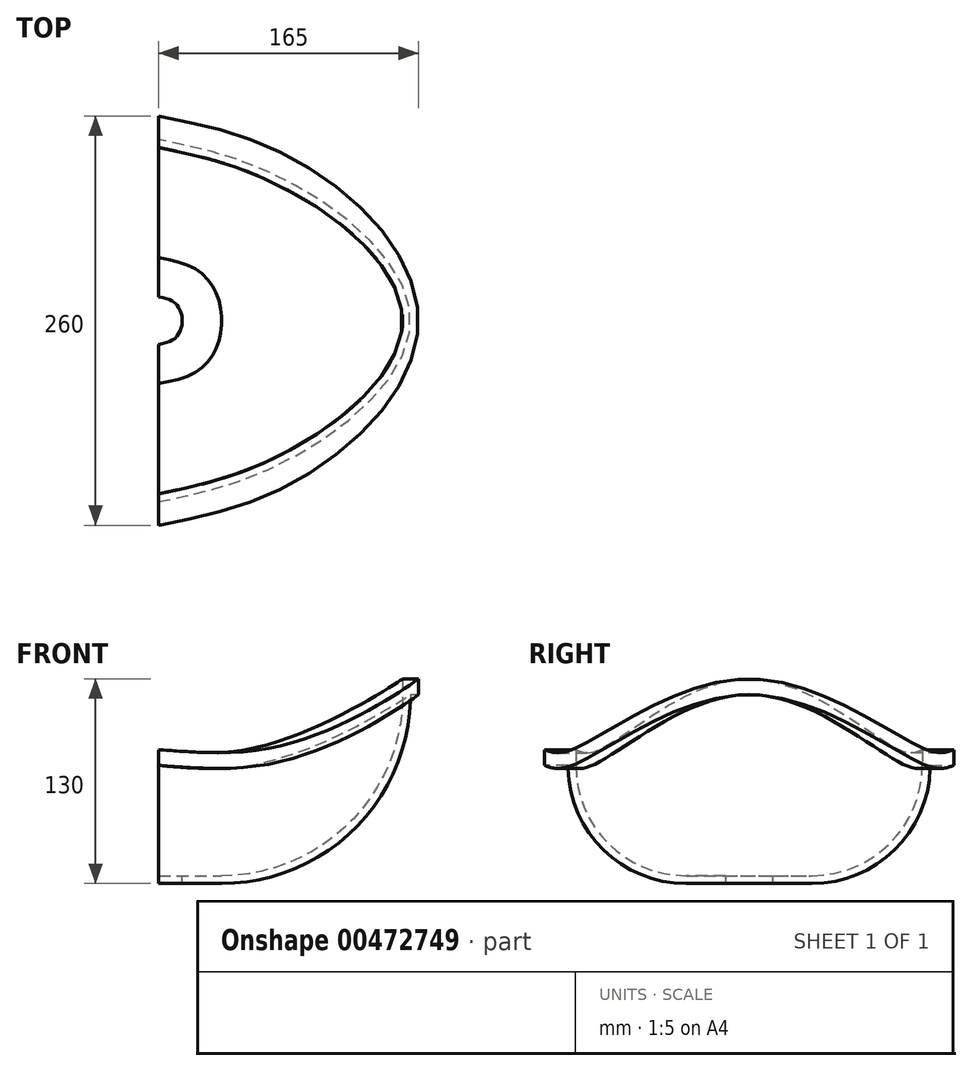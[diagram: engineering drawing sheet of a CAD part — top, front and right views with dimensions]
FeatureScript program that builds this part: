
annotation { "Feature Type Name" : "Feature", "Feature Type Description" : "" }
export const myFeature = defineFeature(function(context is Context, id is Id, definition is map)
    precondition{}
    {
        {
            var Q0;
            Q0=qCreatedBy(makeId("Front.planeOp"),FACE);
            var sketch = newSketch(context, id + "F0", { "sketchPlane" : qUnion([Q0])});
            skLineSegment(sketch, "E0.bottom", {"start": v(15, 5) * mm, "end": v(40, 5) * mm});
            skLineSegment(sketch, "E0.top", {"start": v(15, 0) * mm, "end": v(40, 0) * mm});
            skLineSegment(sketch, "E0.left", {"start": v(15, 5) * mm, "end": v(15, 0) * mm});
            skLineSegment(sketch, "E0.right", {"start": v(40, 5) * mm, "end": v(40, 0) * mm});
            skLineSegment(sketch, "E1.bottom", {"start": v(155, 130) * mm, "end": v(165, 130) * mm});
            skLineSegment(sketch, "E1.top", {"start": v(155, 120) * mm, "end": v(165, 120) * mm});
            skLineSegment(sketch, "E1.left", {"start": v(155, 130) * mm, "end": v(155, 120) * mm});
            skLineSegment(sketch, "E1.right", {"start": v(165, 130) * mm, "end": v(165, 120) * mm});
            skArc(sketch, "E2", {"start": v(40, 0) * mm, "mid": v(124.85, 35.15) * mm, "end": v(160, 120) * mm});
            skArc(sketch, "E3", {"start": v(40, 5) * mm, "mid": v(121.32, 38.68) * mm, "end": v(155, 120) * mm});
            skLineSegment(sketch, "E4", {"start": v(0, 0) * mm, "end": v(0, 50) * mm, "construction": true});
            skSolve(sketch);
        }
        {
            var Q0;
            Q0=sQuery(id+"F0.wireOp",EDGE,"E4");
            cPlane(context, id + "F1", {"entities" : qUnion([Q0]), "cplaneType" : CPlaneType.LINE_ANGLE, "offset" : 25 * mm, "angle" : 30 * degree, "oppositeDirection" : true, "width" : 150 * mm, "height" : 150 * mm});
        }
        {
            var Q0;
            Q0=qCreatedBy(id+"F1.planeOp",FACE);
            var sketch = newSketch(context, id + "F2", { "sketchPlane" : qUnion([Q0])});
            skLineSegment(sketch, "E5.bottom", {"start": v(15, 5) * mm, "end": v(40, 5) * mm});
            skLineSegment(sketch, "E5.top", {"start": v(15, 0) * mm, "end": v(40, 0) * mm});
            skLineSegment(sketch, "E5.left", {"start": v(15, 5) * mm, "end": v(15, 0) * mm});
            skLineSegment(sketch, "E5.right", {"start": v(40, 5) * mm, "end": v(40, 0) * mm});
            skLineSegment(sketch, "E6.bottom", {"start": v(110, 85) * mm, "end": v(130, 85) * mm});
            skLineSegment(sketch, "E6.top", {"start": v(110, 75) * mm, "end": v(130, 75) * mm});
            skLineSegment(sketch, "E6.left", {"start": v(110, 85) * mm, "end": v(110, 75) * mm});
            skLineSegment(sketch, "E6.right", {"start": v(130, 85) * mm, "end": v(130, 75) * mm});
            skArc(sketch, "E7", {"start": v(40, 0) * mm, "mid": v(93.03, 21.97) * mm, "end": v(115, 75) * mm});
            skArc(sketch, "E8", {"start": v(40, 5) * mm, "mid": v(89.5, 25.5) * mm, "end": v(110, 75) * mm});
            skLineSegment(sketch, "E9", {"start": v(0, 0) * mm, "end": v(0, 50) * mm, "construction": true});
            skSolve(sketch);
        }
        {
            var Q0;
            Q0=sQuery(id+"F2.wireOp",EDGE,"E9");
            cPlane(context, id + "F3", {"entities" : qUnion([Q0]), "cplaneType" : CPlaneType.LINE_ANGLE, "offset" : 25 * mm, "angle" : 150 * degree, "oppositeDirection" : true, "width" : 150 * mm, "height" : 150 * mm});
        }
        {
            var Q0;
            Q0=qCreatedBy(id+"F3.planeOp",FACE);
            var sketch = newSketch(context, id + "F4", { "sketchPlane" : qUnion([Q0])});
            skLineSegment(sketch, "E10.bottom", {"start": v(15, 5) * mm, "end": v(40, 5) * mm});
            skLineSegment(sketch, "E10.top", {"start": v(15, 0) * mm, "end": v(40, 0) * mm});
            skLineSegment(sketch, "E10.left", {"start": v(15, 5) * mm, "end": v(15, 0) * mm});
            skLineSegment(sketch, "E10.right", {"start": v(40, 5) * mm, "end": v(40, 0) * mm});
            skLineSegment(sketch, "E11.bottom", {"start": v(110, 85) * mm, "end": v(130, 85) * mm});
            skLineSegment(sketch, "E11.top", {"start": v(110, 75) * mm, "end": v(130, 75) * mm});
            skLineSegment(sketch, "E11.left", {"start": v(110, 85) * mm, "end": v(110, 75) * mm});
            skLineSegment(sketch, "E11.right", {"start": v(130, 85) * mm, "end": v(130, 75) * mm});
            skArc(sketch, "E12", {"start": v(40, 0) * mm, "mid": v(93.03, 21.97) * mm, "end": v(115, 75) * mm});
            skArc(sketch, "E13", {"start": v(40, 5) * mm, "mid": v(89.5, 25.5) * mm, "end": v(110, 75) * mm});
            skLineSegment(sketch, "E14", {"start": v(0, 0) * mm, "end": v(0, 50) * mm, "construction": true});
            skSolve(sketch);
        }
        {
            var Q0;
            Q0=qCreatedBy(makeId("Right.planeOp"),FACE);
            var sketch = newSketch(context, id + "F5", { "sketchPlane" : qUnion([Q0])});
            skLineSegment(sketch, "E15.bottom", {"start": v(15, 5) * mm, "end": v(40, 5) * mm});
            skLineSegment(sketch, "E15.top", {"start": v(15, 0) * mm, "end": v(40, 0) * mm});
            skLineSegment(sketch, "E15.left", {"start": v(15, 5) * mm, "end": v(15, 0) * mm});
            skLineSegment(sketch, "E15.right", {"start": v(40, 5) * mm, "end": v(40, 0) * mm});
            skLineSegment(sketch, "E16.bottom", {"start": v(110, 85) * mm, "end": v(130, 85) * mm});
            skLineSegment(sketch, "E16.top", {"start": v(110, 75) * mm, "end": v(130, 75) * mm});
            skLineSegment(sketch, "E16.left", {"start": v(110, 85) * mm, "end": v(110, 75) * mm});
            skLineSegment(sketch, "E16.right", {"start": v(130, 85) * mm, "end": v(130, 75) * mm});
            skArc(sketch, "E17", {"start": v(40, 0) * mm, "mid": v(93.03, 21.97) * mm, "end": v(115, 75) * mm});
            skArc(sketch, "E18", {"start": v(40, 5) * mm, "mid": v(89.5, 25.5) * mm, "end": v(110, 75) * mm});
            skLineSegment(sketch, "E19", {"start": v(0, 0) * mm, "end": v(0, 50) * mm, "construction": true});
            skSolve(sketch);
        }
        {
            var Q0;
            Q0=sQuery(id+"F5.wireOp",EDGE,"E19");
            cPlane(context, id + "F6", {"entities" : qUnion([Q0]), "cplaneType" : CPlaneType.LINE_ANGLE, "offset" : 25 * mm, "angle" : 180 * degree, "width" : 150 * mm, "height" : 150 * mm});
        }
        {
            var Q0;
            Q0=qCreatedBy(id+"F6.planeOp",FACE);
            var sketch = newSketch(context, id + "F7", { "sketchPlane" : qUnion([Q0])});
            skLineSegment(sketch, "E20.bottom", {"start": v(15, 5) * mm, "end": v(40, 5) * mm});
            skLineSegment(sketch, "E20.top", {"start": v(15, 0) * mm, "end": v(40, 0) * mm});
            skLineSegment(sketch, "E20.left", {"start": v(15, 5) * mm, "end": v(15, 0) * mm});
            skLineSegment(sketch, "E20.right", {"start": v(40, 5) * mm, "end": v(40, 0) * mm});
            skLineSegment(sketch, "E21.bottom", {"start": v(110, 85) * mm, "end": v(130, 85) * mm});
            skLineSegment(sketch, "E21.top", {"start": v(110, 75) * mm, "end": v(130, 75) * mm});
            skLineSegment(sketch, "E21.left", {"start": v(110, 85) * mm, "end": v(110, 75) * mm});
            skLineSegment(sketch, "E21.right", {"start": v(130, 85) * mm, "end": v(130, 75) * mm});
            skArc(sketch, "E22", {"start": v(40, 0) * mm, "mid": v(93.03, 21.97) * mm, "end": v(115, 75) * mm});
            skArc(sketch, "E23", {"start": v(40, 5) * mm, "mid": v(89.5, 25.5) * mm, "end": v(110, 75) * mm});
            skLineSegment(sketch, "E24", {"start": v(0, 0) * mm, "end": v(0, 50) * mm, "construction": true});
            skSolve(sketch);
        }
        {
            var Q0;
            Q0 = qSketchRegion(id + "F7", true);
            var Q1;
            Q1 = qSketchRegion(id + "F4", true);
            var Q2;
            Q2 = qSketchRegion(id + "F0", true);
            var Q3;
            Q3 = qSketchRegion(id + "F2", true);
            var Q4;
            Q4 = qSketchRegion(id + "F5", true);
            loft(context, id + "F8", {"sheetProfilesArray" : [{ "sheetProfileEntities" : qUnion([Q0]) }, { "sheetProfileEntities" : qUnion([Q1]) }, { "sheetProfileEntities" : qUnion([Q2]) }, { "sheetProfileEntities" : qUnion([Q3]) }, { "sheetProfileEntities" : qUnion([Q4]) }]});
        }
    });
